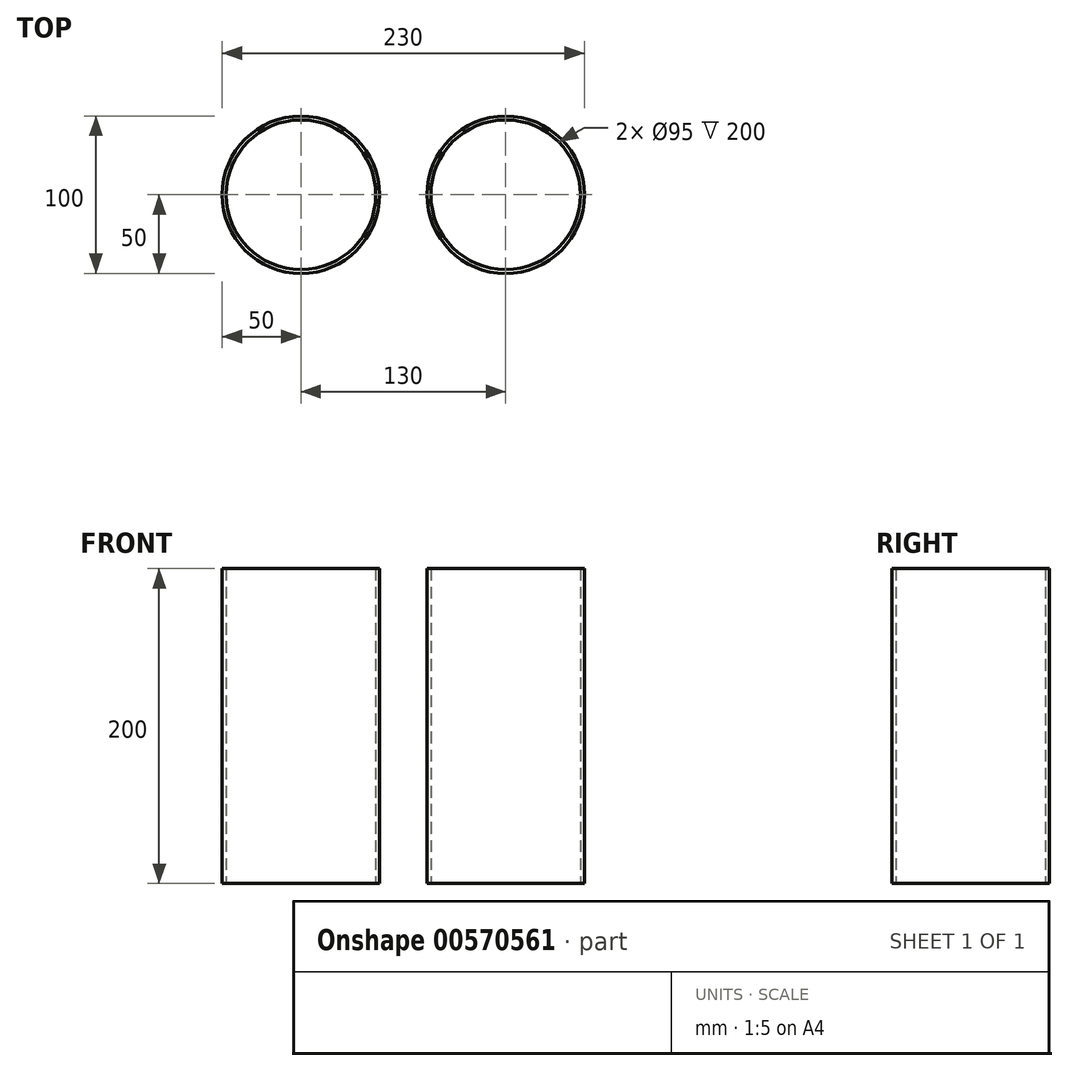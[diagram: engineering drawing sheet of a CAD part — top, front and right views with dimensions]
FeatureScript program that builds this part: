
annotation { "Feature Type Name" : "Feature", "Feature Type Description" : "" }
export const myFeature = defineFeature(function(context is Context, id is Id, definition is map)
    precondition{}
    {
        {
            var Q0;
            Q0=qCreatedBy(makeId("Top.planeOp"),FACE);
            var sketch = newSketch(context, id + "F0", { "sketchPlane" : qUnion([Q0])});
            skCircle(sketch, "E0", {"center": v(0, 0) * mm, "radius": 50 * mm});
            skCircle(sketch, "E1", {"center": v(130, 0) * mm, "radius": 50 * mm});
            skCircle(sketch, "E2", {"center": v(0, 0) * mm, "radius": 47.5 * mm});
            skCircle(sketch, "E3", {"center": v(130, 0) * mm, "radius": 47.5 * mm});
            skSolve(sketch);
        }
        {
            var Q0;
            Q0 = qSketchRegion(id + "F0", true);
            extrude(context, id + "F1", {"entities" : qUnion([Q0]), "depth" : 200 * mm, "offsetDistance" : 25.4 * mm});
        }
    });
